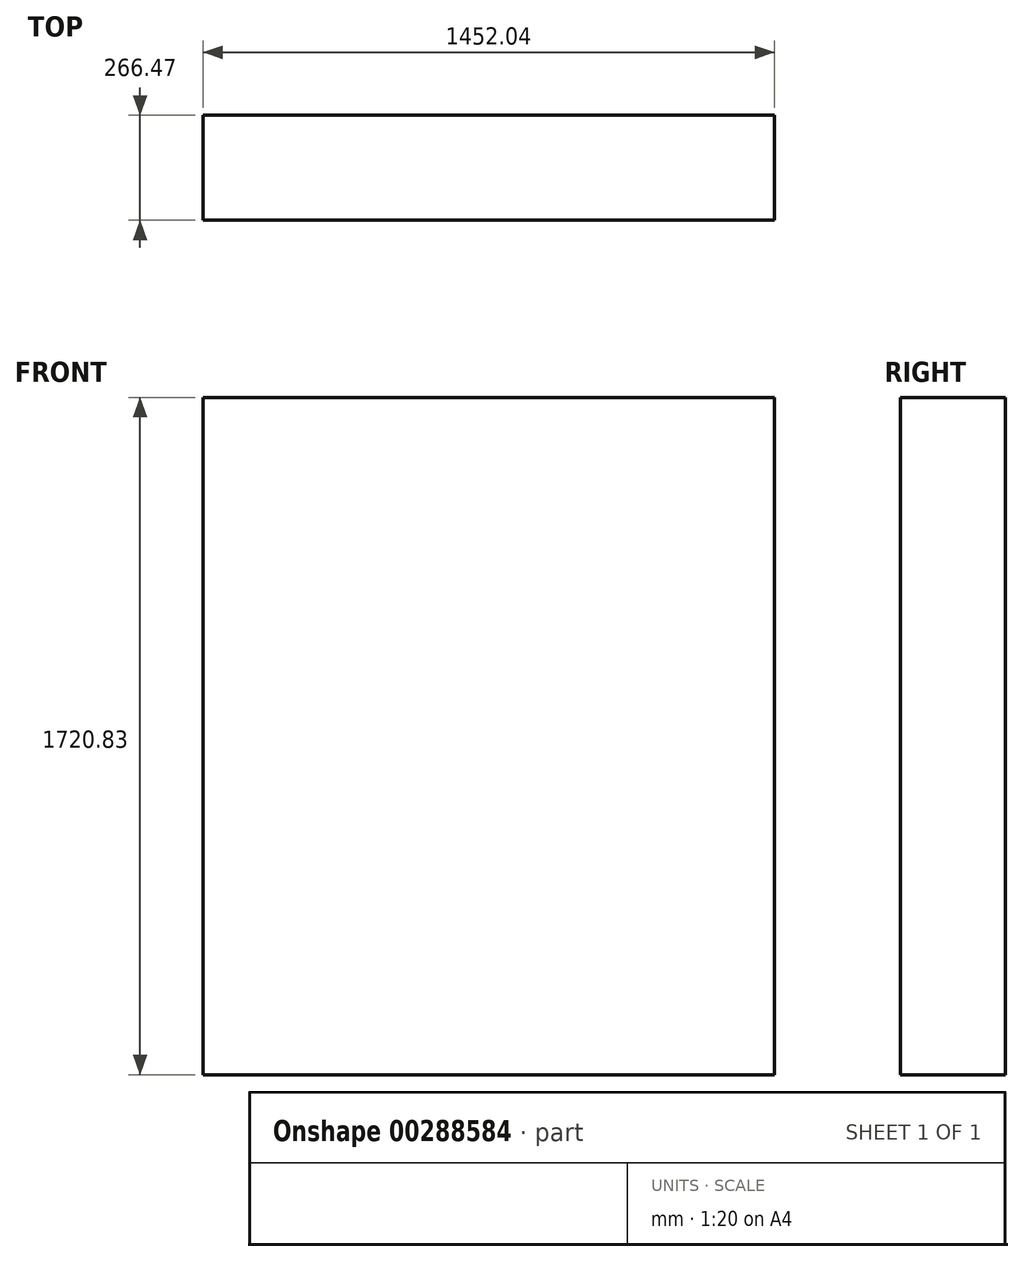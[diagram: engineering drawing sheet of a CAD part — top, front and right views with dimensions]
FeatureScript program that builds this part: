
annotation { "Feature Type Name" : "Feature", "Feature Type Description" : "" }
export const myFeature = defineFeature(function(context is Context, id is Id, definition is map)
    precondition{}
    {
        {
            var Q0;
            Q0=qCreatedBy(makeId("Front.planeOp"),FACE);
            var sketch = newSketch(context, id + "F0", { "sketchPlane" : qUnion([Q0])});
            skLineSegment(sketch, "E0.bottom", {"start": v(706.15, 570.78) * mm, "end": v(-745.9, 570.78) * mm});
            skLineSegment(sketch, "E0.top", {"start": v(706.15, -1150.05) * mm, "end": v(-745.9, -1150.05) * mm});
            skLineSegment(sketch, "E0.left", {"start": v(706.15, 570.78) * mm, "end": v(706.15, -1150.05) * mm});
            skLineSegment(sketch, "E0.right", {"start": v(-745.9, 570.78) * mm, "end": v(-745.9, -1150.05) * mm});
            skSolve(sketch);
        }
        {
            var Q0;
            Q0=makeQuery(id+"F0.imprint","IMPRINT",FACE,{"disambiguationData":[TD([[makeQuery(id+"F0.imprint","IMPRINT",EDGE,{"derivedFrom":sQuery(id+"F0.wireOp",EDGE,"E0.bottom")}),1.0]])]});
            extrude(context, id + "F1", {"entities" : qUnion([Q0]), "depth" : 266.47 * mm});
        }
    });
